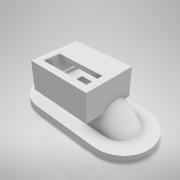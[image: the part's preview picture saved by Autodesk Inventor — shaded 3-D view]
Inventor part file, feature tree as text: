
AUTODESK INVENTOR PART (.ipt)
format: ipt  version: 2020 (Build 240168000, 168)  size: 495,104 bytes
history: native  units: mm
features: sketch x10, extrude x7, plane x5, chamfer x4, projected_geometry x3, other x2, thicken_offset x1, fillet x1, loft x1
ambient origin geometry x8: Origin, YZ Plane, XZ Plane, XY Plane, X Axis, Y Axis, Z Axis, Center Point
bodies: Solid1 (feature_tree)
feature tree (34):
  extrude  "Extrusion1"  Depth=20.7mm
  extrude  "Extrusion2"  Depth=15.24mm
  extrude  "Extrusion3"  Depth=2.0mm
  chamfer  "Chamfer2"  Distance=2.0mm
  chamfer  "Chamfer3"  Distance=2.5mm
  chamfer  "Chamfer4"  Distance=2.0mm Angle=45.0deg
  chamfer  "Chamfer5"  Distance=2.0mm Angle=45.0deg
  plane  "Work Plane3"
  sketch  "Sketch7"  dims[d28=3.0mm]
  plane  "Work Plane4"
  sketch  "Sketch8"  dims[d29=10.0mm d30=2.0mm d31=0.0mm d32=0.0mm]
  plane  "Work Plane5"
  sketch  "Sketch12"  dims[d33=1.5mm]
  thicken_offset  "Thicken1"
  plane  "Work Plane6"
  extrude  "Extrusion4"  Depth=2.0mm TaperAngle=45.0deg
  extrude  "Extrusion5"  Depth=10.0mm
  fillet  "Fillet3"  Radius=30.0mm
  extrude  "Extrusion7"  TaperAngle=0.0deg  [1 undecoded]
  plane  "Work Plane7"
  extrude  "Extrusion8"  TaperAngle=0.0deg  [1 undecoded]
  sketch  "Sketch1"  dims[d6=20.7mm d15=2.0mm]
  other  "Image1"
  sketch  "Sketch2"  dims[d16=2.0mm d17=15.24mm]
  sketch  "Sketch3"  dims[d22=2.0mm d23=2.0mm d24=2.0mm d25=0.0mm]
  other  "Srf1"
  sketch  "Sketch13"  dims[d34=1.5mm d35=2.5mm d36=0.0mm d40=2.0mm d41=1.5mm d42=45.0deg d43=2.0mm d44=2.0mm d45=45.0deg]
  sketch  "Sketch14"  dims[d46=2.0mm d47=2.5mm d48=45.0deg d49=2.0mm d50=2.5mm d51=45.0deg]
  sketch  "Sketch15"  dims[d65=-1.0mm d66=10.0mm d67=30.0mm]
  sketch  "Sketch18"  dims[d68=-1.0mm d75=0.0mm d76=90.0deg d77=0.0mm d78=90.0deg d79=2.0mm d80=2.0mm d81=1.0mm d82=8.0mm d83=2.0mm d84=0.0mm d87=2.3mm d88=2.3mm d89=2.0mm d90=2.0mm d91=2.0mm d92=0.0mm d93=0.3mm d104=2.0mm d105=0.0mm d109=5.0mm d112=5.137334mm d113=11.0mm d116=6.5mm d117=1.0mm d118=5.0mm d119=0.0mm d114=0.872665mm d115=0.5mm]
  projected_geometry  "Projected Loop1"
  projected_geometry  "Projected Loop2"
  projected_geometry  "Projected Loop3"
  loft  "LoftSrf1"
note: 2 required parameter values undecoded (feature->parameter linkage not recoverable at this tier; creation-order binding heuristic only, values carry confidence <= 0.55)
